# Revit family: Sanitary_Accessories_hansgrohe_26273007-Vernis-Blend-Shower-holder-set_
name_source: partatom
category: Furniture
revit_build: Autodesk Revit 2015 (Build: 20140903_1530(x64)
units: mm (PartAtom-declared; Revit-internal decimal feet)

## types (1)
- Chrome 000
    BIMobject category = Accessories
    BIMobject category code = sanitary-accessories1
    BIMobject main category = Sanitary
    BIMobject main category code = sanitary
    Brand url = http://www.hansgrohe-int.com
    Design country = Germany
    Edition number = 1
    IFC Classification = Sanitary Terminal
    Installation instructions = https://www.hansgrohe-usa.com
    Manufacturer country = Germany
    Manufacturer name = hansgrohe
    Masterformat 2014 Code = 22 41 23
    Masterformat 2014 Description = Residential Showers
    Material main = Chrome
    Material secondary = Chrome
    NBS Reference Code = 35-06-82
    NBS Reference Description = Shower Mixers
    Product Guid = 5348852d-1c60-4cd2-a160-7ab33c8fd56f
    Product SKU = 26273007
    Product data url = https://bimobject.com
    Product family = Vernis
    Product group = Porter sets
    Product name = 26273007 Vernis Blend Shower holder set Vario with shower hose 160 cm
    Product url = https://www.hansgrohe-usa.com
    QR code = http://bimobject.com
    Technical description = https://www.hansgrohe-usa.com
    UNSPSC Code = 30181503
    Uniclass 1.4 Code = L7214
    Uniclass 1.4 Description = Showers
    Uniclass 2.0 Code = PR-35-06-81
    Uniclass 2.0 Description = Shower Heads
    Uniclass 2015 Code = Pr_40_20_87_77
    Uniclass 2015 Name = Shower head holders
    Uniformat II Code = D2010
    Uniformat II Description = Plumbing Fixtures

## geometry (parser evidence)
native form markers: Blend x2, Sweep x2
no freeform markers — native parametric forms only
